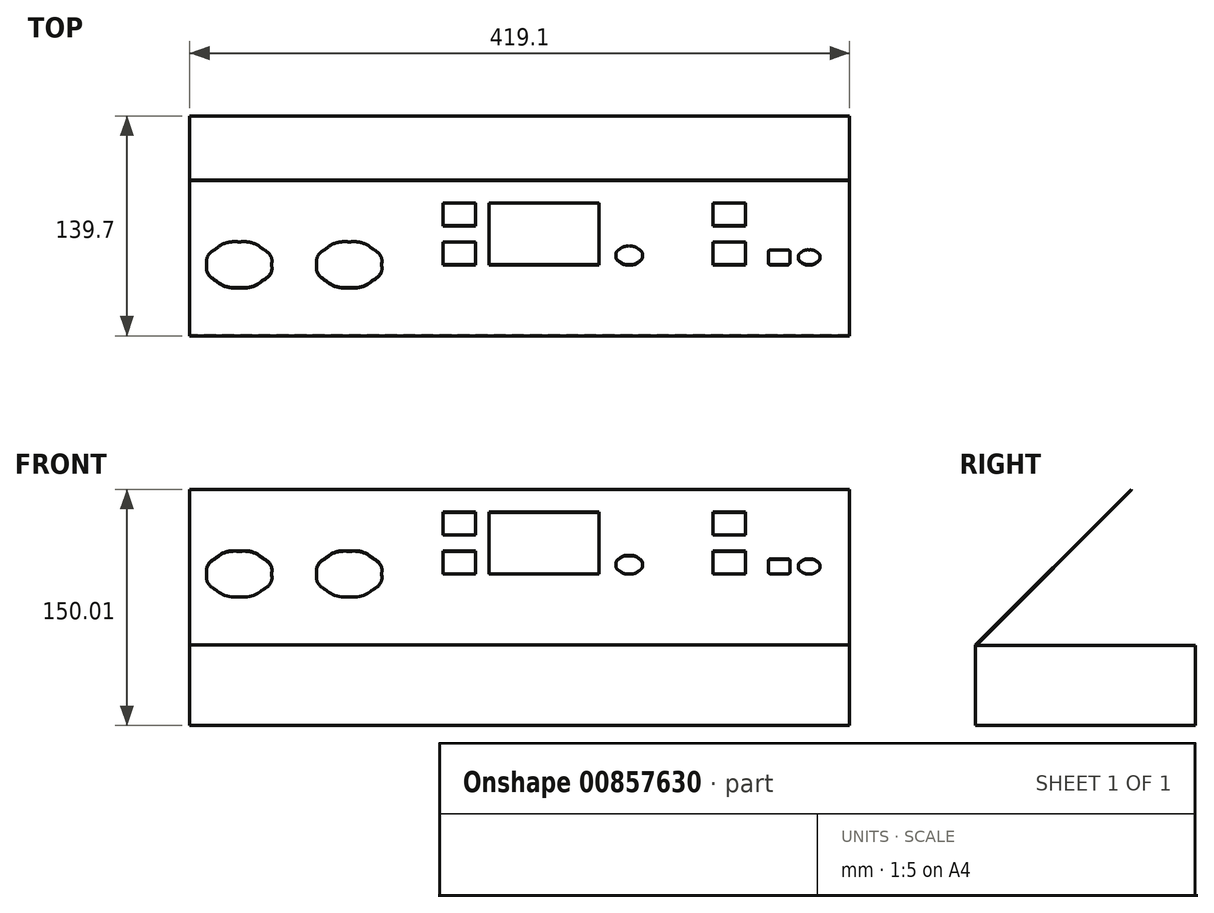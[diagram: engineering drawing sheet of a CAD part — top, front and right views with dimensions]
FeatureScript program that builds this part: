
annotation { "Feature Type Name" : "Feature", "Feature Type Description" : "" }
export const myFeature = defineFeature(function(context is Context, id is Id, definition is map)
    precondition{}
    {
        {
            var Q0;
            Q0=qCreatedBy(makeId("Right.planeOp"),FACE);
            var sketch = newSketch(context, id + "F0", { "sketchPlane" : qUnion([Q0])});
            skLineSegment(sketch, "E0.bottom", {"start": v(0, 0) * mm, "end": v(-139.7, 0) * mm});
            skLineSegment(sketch, "E0.top", {"start": v(0, 50.8) * mm, "end": v(-139.3, 50.8) * mm});
            skLineSegment(sketch, "E0.left", {"start": v(0, 0) * mm, "end": v(0, 50.8) * mm});
            skLineSegment(sketch, "E0.right", {"start": v(-139.7, 0) * mm, "end": v(-139.7, 51.22) * mm});
            skLineSegment(sketch, "E1", {"start": v(-139.7, 51.22) * mm, "end": v(-40.92, 150) * mm});
            skLineSegment(sketch, "E2", {"start": v(-40.92, 150) * mm, "end": v(-40.63, 149.72) * mm});
            skLineSegment(sketch, "E3", {"start": v(-40.63, 149.72) * mm, "end": v(-139.3, 51.05) * mm});
            skLineSegment(sketch, "E4", {"start": v(-139.3, 50.8) * mm, "end": v(-139.3, 51.05) * mm});
            skLineSegment(sketch, "E5", {"start": v(-139.3, 50.8) * mm, "end": v(-139.7, 50.8) * mm, "construction": true});
            skSolve(sketch);
        }
        {
            var Q0;
            Q0=qSketchRegion(id+"F0",true);
            extrude(context, id + "F1", {"entities" : qUnion([Q0]), "endBound" : BoundingType.SYMMETRIC, "depth" : 419.1 * mm, "offsetDistance" : 25.4 * mm});
        }
        {
            var Q0;
            Q0=makeQuery(id+"F1.opExtrude","SWEPT_FACE",FACE,{"disambiguationData":[OSD([sQuery(id+"F0.wireOp",EDGE,"E1")])]});
            var sketch = newSketch(context, id + "F2", { "sketchPlane" : qUnion([Q0])});
            skLineSegment(sketch, "E6", {"start": v(50.44, 1.24) * mm, "end": v(50.44, 56.8) * mm});
            skLineSegment(sketch, "E7", {"start": v(50.44, 56.8) * mm, "end": v(-19.4, 56.8) * mm});
            skLineSegment(sketch, "E8", {"start": v(-19.4, 56.8) * mm, "end": v(-19.4, 1.24) * mm});
            skLineSegment(sketch, "E9", {"start": v(-19.4, 1.24) * mm, "end": v(50.44, 1.24) * mm});
            skLineSegment(sketch, "E10", {"start": v(-28.14, 1.24) * mm, "end": v(-28.14, 21.88) * mm});
            skLineSegment(sketch, "E11", {"start": v(-48.78, 21.88) * mm, "end": v(-48.78, 1.24) * mm});
            skLineSegment(sketch, "E12", {"start": v(-48.78, 21.88) * mm, "end": v(-28.14, 21.88) * mm});
            skLineSegment(sketch, "E13", {"start": v(-48.78, 1.24) * mm, "end": v(-28.14, 1.24) * mm});
            skLineSegment(sketch, "E14", {"start": v(-48.78, 36.17) * mm, "end": v(-28.14, 36.17) * mm});
            skLineSegment(sketch, "E15", {"start": v(-48.78, 56.8) * mm, "end": v(-28.14, 56.8) * mm});
            skLineSegment(sketch, "E16", {"start": v(-48.78, 56.8) * mm, "end": v(-48.78, 36.17) * mm});
            skLineSegment(sketch, "E17", {"start": v(-28.14, 36.17) * mm, "end": v(-28.14, 56.8) * mm});
            skLineSegment(sketch, "E18", {"start": v(122.67, 56.8) * mm, "end": v(122.67, 36.17) * mm});
            skLineSegment(sketch, "E19", {"start": v(122.67, 21.88) * mm, "end": v(122.67, 1.24) * mm});
            skLineSegment(sketch, "E20", {"start": v(-209.9, -62.26) * mm, "end": v(-209.9, 76.65) * mm, "construction": true});
            skLineSegment(sketch, "E21", {"start": v(169.9, 14.74) * mm, "end": v(159.58, 14.74) * mm});
            skLineSegment(sketch, "E22", {"start": v(171.49, 2.83) * mm, "end": v(171.49, 13.15) * mm});
            skLineSegment(sketch, "E23", {"start": v(169.9, 1.24) * mm, "end": v(159.58, 1.24) * mm});
            skLineSegment(sketch, "E24", {"start": v(209.2, -62.26) * mm, "end": v(209.2, 76.65) * mm, "construction": true});
            skLineSegment(sketch, "E25", {"start": v(143.3, 36.17) * mm, "end": v(143.3, 56.8) * mm});
            skLineSegment(sketch, "E26", {"start": v(143.3, 1.24) * mm, "end": v(143.3, 21.88) * mm});
            skLineSegment(sketch, "E27", {"start": v(158, 13.15) * mm, "end": v(158, 2.83) * mm});
            skLineSegment(sketch, "E28", {"start": v(-209.9, 76.65) * mm, "end": v(209.2, 76.65) * mm, "construction": true});
            skLineSegment(sketch, "E29", {"start": v(122.67, 56.8) * mm, "end": v(143.3, 56.8) * mm});
            skLineSegment(sketch, "E30", {"start": v(122.67, 36.17) * mm, "end": v(143.3, 36.17) * mm});
            skLineSegment(sketch, "E31", {"start": v(122.67, 1.24) * mm, "end": v(143.3, 1.24) * mm});
            skLineSegment(sketch, "E32", {"start": v(122.67, 21.88) * mm, "end": v(143.3, 21.88) * mm});
            skLineSegment(sketch, "E33", {"start": v(209.2, -62.26) * mm, "end": v(-209.9, -62.26) * mm, "construction": true});
            skFitSpline(sketch, "E34", {"points": [v(-108.3, 21.88) * mm, v(-113.71, 21.88) * mm, v(-119.08, 19.66) * mm, v(-122.9, 15.84) * mm]});
            skFitSpline(sketch, "E35", {"points": [v(-122.9, 15.84) * mm, v(-126.72, 12.01) * mm, v(-128.95, 6.65) * mm, v(-128.95, 1.24) * mm, v(-128.95, -4.16) * mm, v(-126.72, -9.53) * mm, v(-122.9, -13.35) * mm]});
            skFitSpline(sketch, "E36", {"points": [v(-122.9, -13.35) * mm, v(-119.08, -17.17) * mm, v(-113.71, -19.4) * mm, v(-108.3, -19.4) * mm, v(-102.9, -19.4) * mm, v(-97.54, -17.17) * mm, v(-93.72, -13.35) * mm]});
            skFitSpline(sketch, "E37", {"points": [v(-93.72, -13.35) * mm, v(-89.9, -9.53) * mm, v(-87.67, -4.16) * mm, v(-87.67, 1.24) * mm, v(-87.67, 6.65) * mm, v(-89.9, 12.01) * mm, v(-93.72, 15.84) * mm]});
            skFitSpline(sketch, "E38", {"points": [v(-93.72, 15.84) * mm, v(-97.54, 19.66) * mm, v(-102.9, 21.88) * mm, v(-108.3, 21.88) * mm]});
            skFitSpline(sketch, "E39", {"points": [v(-178.16, 21.88) * mm, v(-183.56, 21.88) * mm, v(-188.93, 19.66) * mm, v(-192.75, 15.84) * mm]});
            skFitSpline(sketch, "E40", {"points": [v(-192.75, 15.84) * mm, v(-196.57, 12.01) * mm, v(-198.8, 6.65) * mm, v(-198.8, 1.24) * mm, v(-198.8, -4.16) * mm, v(-196.57, -9.53) * mm, v(-192.75, -13.35) * mm]});
            skFitSpline(sketch, "E41", {"points": [v(-192.75, -13.35) * mm, v(-188.93, -17.17) * mm, v(-183.56, -19.4) * mm, v(-178.16, -19.4) * mm, v(-172.76, -19.4) * mm, v(-167.39, -17.17) * mm, v(-163.57, -13.35) * mm]});
            skFitSpline(sketch, "E42", {"points": [v(-163.57, -13.35) * mm, v(-159.75, -9.53) * mm, v(-157.52, -4.16) * mm, v(-157.52, 1.24) * mm, v(-157.52, 6.65) * mm, v(-159.75, 12.01) * mm, v(-163.57, 15.84) * mm]});
            skFitSpline(sketch, "E43", {"points": [v(-163.57, 15.84) * mm, v(-167.39, 19.66) * mm, v(-172.76, 21.88) * mm, v(-178.16, 21.88) * mm]});
            skFitSpline(sketch, "E44", {"points": [v(171.49, 13.15) * mm, v(171.49, 13.56) * mm, v(171.32, 13.98) * mm, v(171.02, 14.27) * mm]});
            skFitSpline(sketch, "E45", {"points": [v(171.02, 14.27) * mm, v(170.73, 14.56) * mm, v(170.32, 14.74) * mm, v(169.9, 14.74) * mm]});
            skFitSpline(sketch, "E46", {"points": [v(169.9, 1.24) * mm, v(170.32, 1.24) * mm, v(170.73, 1.41) * mm, v(171.02, 1.7) * mm]});
            skFitSpline(sketch, "E47", {"points": [v(171.02, 1.7) * mm, v(171.32, 2) * mm, v(171.49, 2.41) * mm, v(171.49, 2.83) * mm]});
            skFitSpline(sketch, "E48", {"points": [v(69.5, 17.91) * mm, v(67.3, 17.91) * mm, v(65.14, 17.01) * mm, v(63.6, 15.47) * mm]});
            skFitSpline(sketch, "E49", {"points": [v(63.6, 15.47) * mm, v(62.05, 13.93) * mm, v(61.16, 11.76) * mm, v(61.16, 9.58) * mm, v(61.16, 7.4) * mm, v(62.05, 5.23) * mm, v(63.6, 3.68) * mm]});
            skFitSpline(sketch, "E50", {"points": [v(63.6, 3.68) * mm, v(65.14, 2.14) * mm, v(67.3, 1.24) * mm, v(69.5, 1.24) * mm, v(71.67, 1.24) * mm, v(73.84, 2.14) * mm, v(75.38, 3.68) * mm]});
            skFitSpline(sketch, "E51", {"points": [v(75.38, 3.68) * mm, v(76.93, 5.23) * mm, v(77.83, 7.4) * mm, v(77.83, 9.58) * mm, v(77.83, 11.76) * mm, v(76.93, 13.93) * mm, v(75.38, 15.47) * mm]});
            skFitSpline(sketch, "E52", {"points": [v(75.38, 15.47) * mm, v(73.84, 17.01) * mm, v(71.67, 17.91) * mm, v(69.5, 17.91) * mm]});
            skFitSpline(sketch, "E53", {"points": [v(183.8, 14.74) * mm, v(182.02, 14.74) * mm, v(180.27, 14) * mm, v(179.02, 12.76) * mm]});
            skFitSpline(sketch, "E54", {"points": [v(179.02, 12.76) * mm, v(177.77, 11.51) * mm, v(177.04, 9.76) * mm, v(177.04, 7.99) * mm, v(177.04, 6.22) * mm, v(177.77, 4.47) * mm, v(179.02, 3.22) * mm]});
            skFitSpline(sketch, "E55", {"points": [v(179.02, 3.22) * mm, v(180.27, 1.97) * mm, v(182.02, 1.24) * mm, v(183.8, 1.24) * mm, v(185.56, 1.24) * mm, v(187.31, 1.97) * mm, v(188.56, 3.22) * mm]});
            skFitSpline(sketch, "E56", {"points": [v(188.56, 3.22) * mm, v(189.81, 4.47) * mm, v(190.54, 6.22) * mm, v(190.54, 7.99) * mm, v(190.54, 9.76) * mm, v(189.81, 11.51) * mm, v(188.56, 12.76) * mm]});
            skFitSpline(sketch, "E57", {"points": [v(188.56, 12.76) * mm, v(187.31, 14) * mm, v(185.56, 14.74) * mm, v(183.8, 14.74) * mm]});
            skFitSpline(sketch, "E58", {"points": [v(158, 2.83) * mm, v(158, 2.41) * mm, v(158.17, 2) * mm, v(158.46, 1.7) * mm]});
            skFitSpline(sketch, "E59", {"points": [v(158.46, 1.7) * mm, v(158.75, 1.41) * mm, v(159.17, 1.24) * mm, v(159.58, 1.24) * mm]});
            skFitSpline(sketch, "E60", {"points": [v(159.58, 14.74) * mm, v(159.17, 14.74) * mm, v(158.75, 14.56) * mm, v(158.46, 14.27) * mm]});
            skFitSpline(sketch, "E61", {"points": [v(158.46, 14.27) * mm, v(158.17, 13.98) * mm, v(158, 13.56) * mm, v(158, 13.15) * mm]});
            skSolve(sketch);
        }
        {
            var Q0;
            Q0=qSketchRegion(id+"F2",true);
            var Q1;
            Q1=makeQuery(id+"F1.opExtrude","SWEPT_FACE",FACE,{"disambiguationData":[OSD([sQuery(id+"F0.wireOp",EDGE,"E3")])]});
            extrude(context, id + "F3", {"entities" : qUnion([Q0]), "operationType" : NewBodyOperationType.REMOVE, "endBound" : BoundingType.UP_TO_SURFACE, "oppositeDirection" : true, "depth" : 25.4 * mm, "endBoundEntityFace" : qUnion([Q1]), "offsetDistance" : 25.4 * mm});
        }
    });
